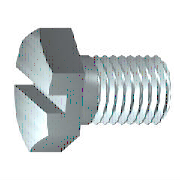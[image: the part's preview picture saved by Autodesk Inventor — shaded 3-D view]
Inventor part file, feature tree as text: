
AUTODESK INVENTOR PART (.ipt)
format: ipt  version: 2019 (Build 230136000, 136)  size: 209,408 bytes
history: native  units: mm (DEFAULTED — no unit token found)
features: sketch x4, extrude x2, chamfer x1, plane x1
ambient origin geometry x7: Origin, YZ Plane, XZ Plane, X Axis, Y Axis, Z Axis, Center Point
bodies: Solid1 (feature_tree), Body (feature_tree)
feature tree (8):
  extrude  "Head"  Depth=4.0mm
  extrude  "Slot"  Depth=2.4mm
  chamfer  "Chamfer1"  Angle=90.0deg  [1 undecoded]
  plane  "Work Plane1"
  sketch  "Sketch1"  dims[d0=8.0mm d1=4.0mm]
  sketch  "Sketch2"  dims[d12=90.0deg d2=2.4mm]
  sketch  "Sketch4"  dims[d4=30.0deg d21=90.0deg d5=0.429415mm d6=0.429515mm d7=0.0mm d8=0.4001mm d9=5.88mm d10=7.0mm d11=1.2mm d13=1.0mm d36=10.0mm d14=0.0mm d15=7.3mm d16=0.0mm d17=7.0mm d46=45.0deg d49=0.0mm d50=0.0mm]
  sketch  "Sketch3"  dims[d3=0.0mm]
note: 1 required parameter value undecoded (feature->parameter linkage not recoverable at this tier; creation-order binding heuristic only, values carry confidence <= 0.55)
